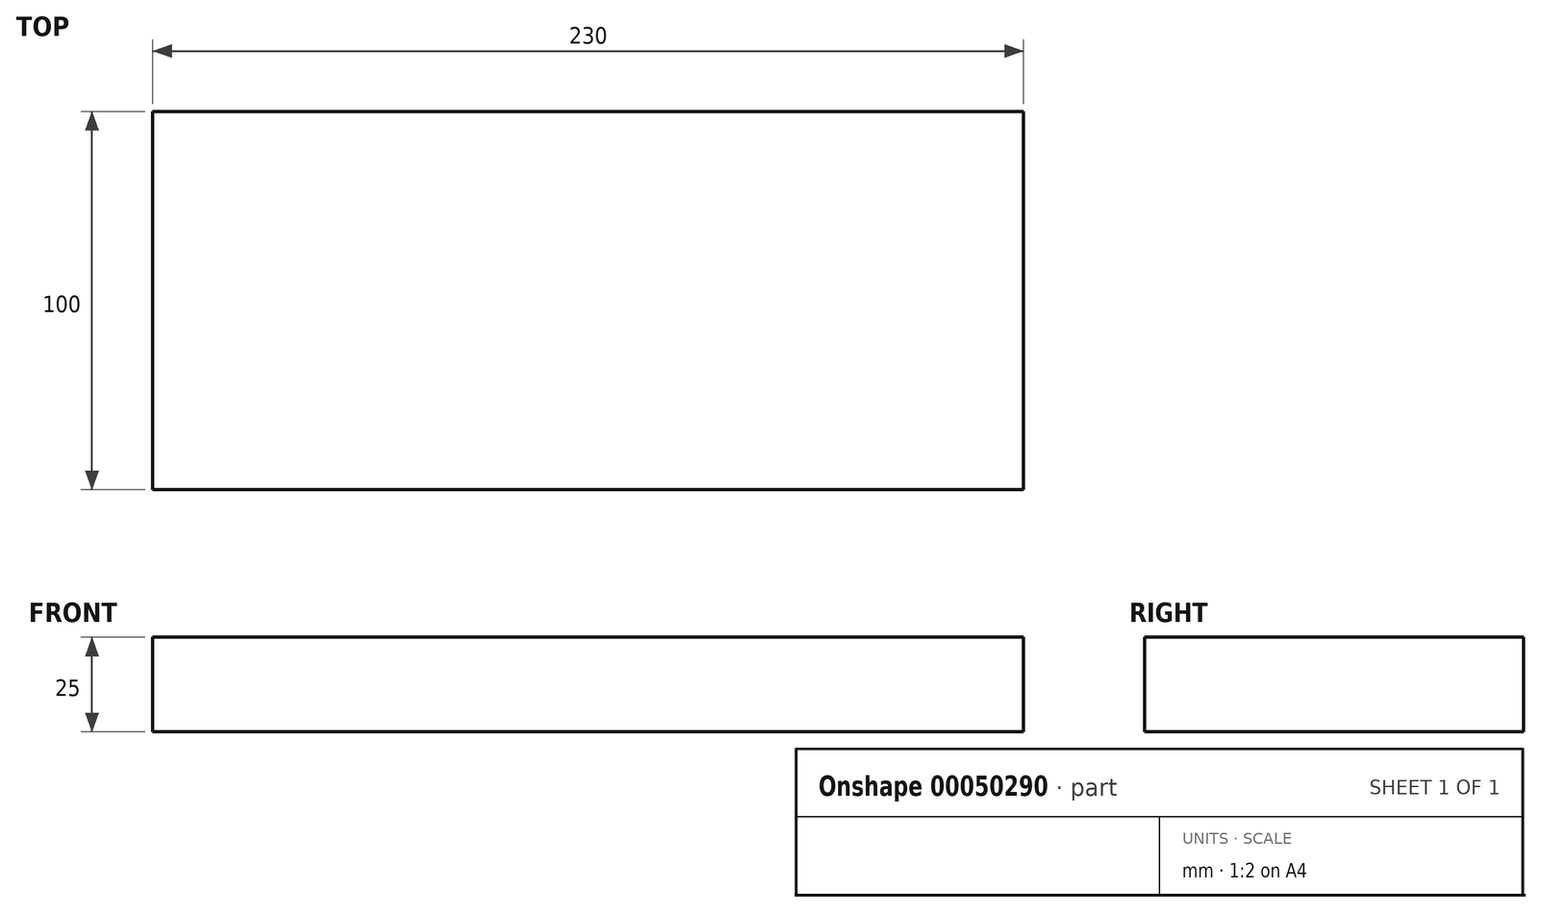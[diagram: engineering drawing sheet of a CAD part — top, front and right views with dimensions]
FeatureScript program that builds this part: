
annotation { "Feature Type Name" : "Feature", "Feature Type Description" : "" }
export const myFeature = defineFeature(function(context is Context, id is Id, definition is map)
    precondition{}
    {
        {
            var Q0;
            Q0=qCreatedBy(makeId("Top.planeOp"),FACE);
            var sketch = newSketch(context, id + "F0", { "sketchPlane" : qUnion([Q0])});
            skLineSegment(sketch, "E0.rect.bottom", {"start": v(115, 50) * mm, "end": v(-115, 50) * mm});
            skLineSegment(sketch, "E0.rect.top", {"start": v(115, -50) * mm, "end": v(-115, -50) * mm});
            skLineSegment(sketch, "E0.rect.left", {"start": v(115, 50) * mm, "end": v(115, -50) * mm});
            skLineSegment(sketch, "E0.rect.right", {"start": v(-115, 50) * mm, "end": v(-115, -50) * mm});
            skPoint(sketch, "E0.rect.middle", {"position": v(0, 0) * mm});
            skSolve(sketch);
        }
        {
            var Q0;
            Q0=makeQuery(id+"F0.imprint","IMPRINT",FACE,{"disambiguationData":[TD([[makeQuery(id+"F0.imprint","IMPRINT",EDGE,{"derivedFrom":sQuery(id+"F0.wireOp",EDGE,"E0.rect.bottom")}),1.0]])]});
            extrude(context, id + "F1", {"entities" : qUnion([Q0]), "depth" : 25 * mm});
        }
    });
